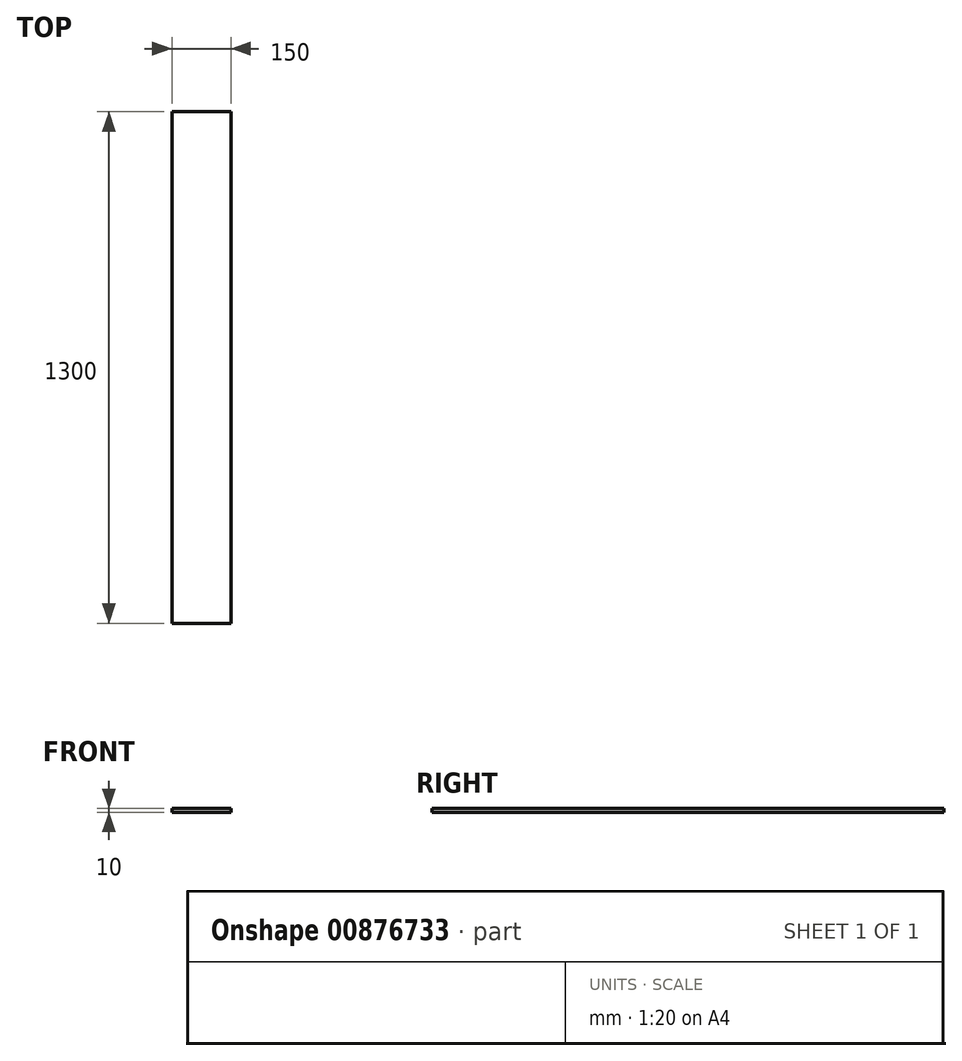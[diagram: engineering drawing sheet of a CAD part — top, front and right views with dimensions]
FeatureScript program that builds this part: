
annotation { "Feature Type Name" : "Feature", "Feature Type Description" : "" }
export const myFeature = defineFeature(function(context is Context, id is Id, definition is map)
    precondition{}
    {
        {
            var Q0;
            Q0=qCreatedBy(makeId("Top.planeOp"),FACE);
            var sketch = newSketch(context, id + "F0", { "sketchPlane" : qUnion([Q0])});
            skLineSegment(sketch, "E0.bottom", {"start": v(75, 650) * mm, "end": v(-75, 650) * mm});
            skLineSegment(sketch, "E0.top", {"start": v(75, -650) * mm, "end": v(-75, -650) * mm});
            skLineSegment(sketch, "E0.left", {"start": v(75, 650) * mm, "end": v(75, -650) * mm});
            skLineSegment(sketch, "E0.right", {"start": v(-75, 650) * mm, "end": v(-75, -650) * mm});
            skPoint(sketch, "E0.middle", {"position": v(0, 0) * mm});
            skSolve(sketch);
        }
        {
            var Q0;
            Q0=makeQuery(id+"F0.imprint","IMPRINT",FACE,{"disambiguationData":[TD([[makeQuery(id+"F0.imprint","IMPRINT",EDGE,{"derivedFrom":sQuery(id+"F0.wireOp",EDGE,"E0.bottom")}),1.0]])]});
            extrude(context, id + "F1", {"entities" : qUnion([Q0]), "depth" : 10 * mm, "offsetDistance" : 25 * mm});
        }
    });
